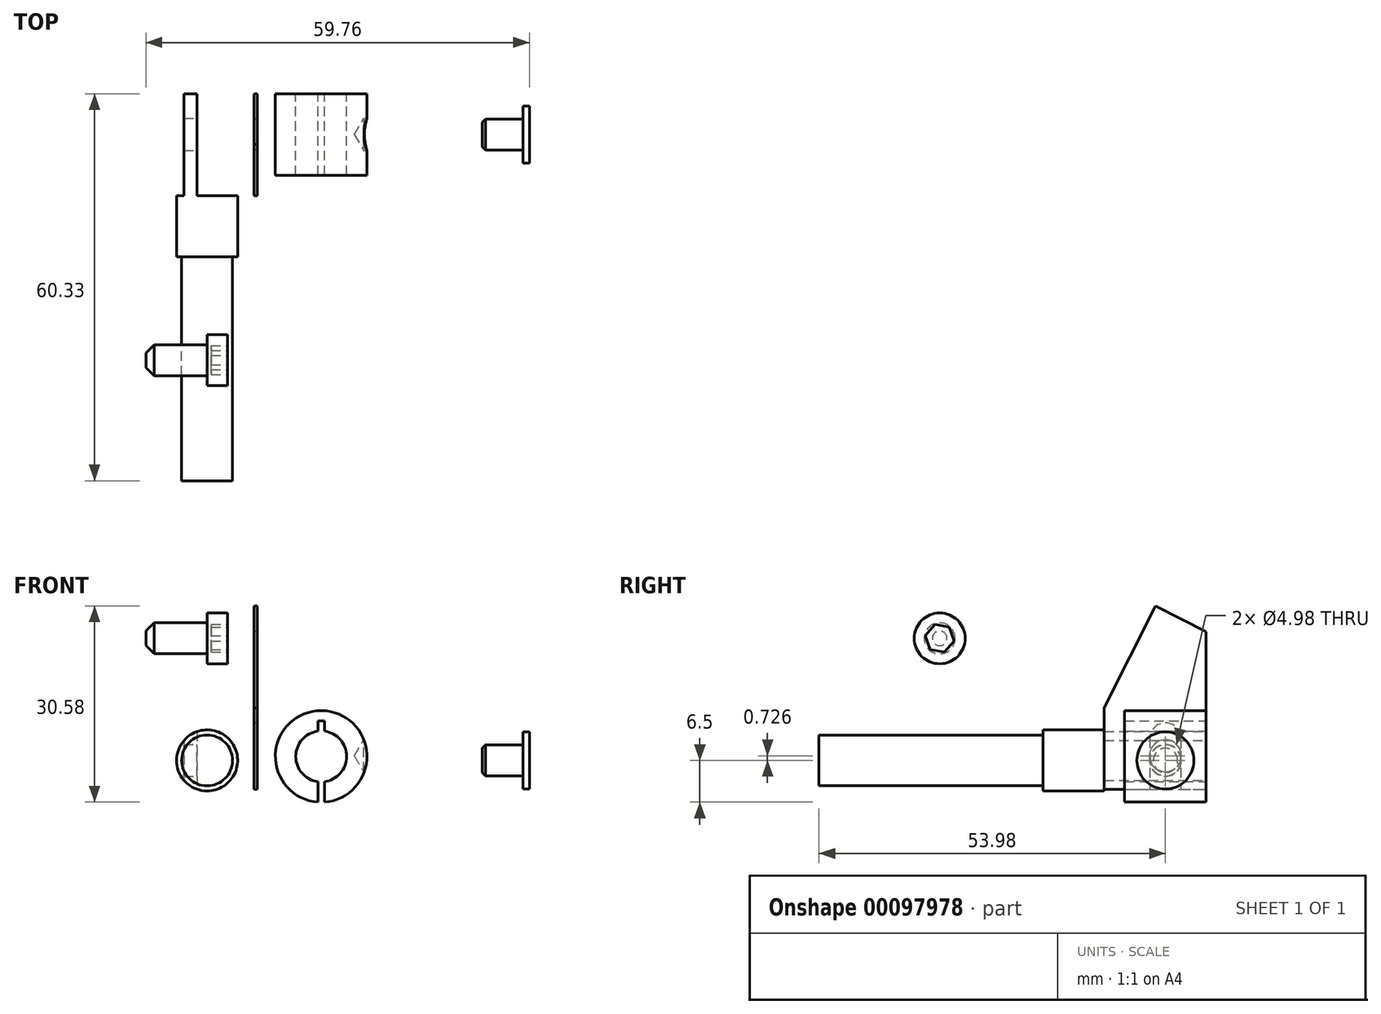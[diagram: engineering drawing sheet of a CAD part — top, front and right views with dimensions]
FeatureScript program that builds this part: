
annotation { "Feature Type Name" : "Feature", "Feature Type Description" : "" }
export const myFeature = defineFeature(function(context is Context, id is Id, definition is map)
    precondition{}
    {
        {
            var Q0;
            Q0=qCreatedBy(makeId("Front.planeOp"),FACE);
            var sketch = newSketch(context, id + "F0", { "sketchPlane" : qUnion([Q0])});
            skCircle(sketch, "E0", {"center": v(0, 0) * mm, "radius": 4.76 * mm});
            skSolve(sketch);
        }
        {
            var Q0;
            Q0=makeQuery(id+"F0.imprint","IMPRINT",FACE,{"disambiguationData":[TD([[makeQuery(id+"F0.imprint","IMPRINT",EDGE,{"derivedFrom":sQuery(id+"F0.wireOp",EDGE,"E0")}),1.0]])]});
            extrude(context, id + "F1", {"entities" : qUnion([Q0]), "depth" : 25.4 * mm});
        }
        {
            var Q0;
            Q0=makeQuery(id+"F1.opExtrude","CAP_FACE",FACE,{"disambiguationData":[OSD([sQuery(id+"F0.wireOp",EDGE,"E0")])],"isStart":false});
            var sketch = newSketch(context, id + "F2", { "sketchPlane" : qUnion([Q0])});
            skCircle(sketch, "E1.0", {"center": v(0, 0) * mm, "radius": 4.76 * mm, "construction": true});
            skCircle(sketch, "E2", {"center": v(0, 0) * mm, "radius": 3.96 * mm});
            skSolve(sketch);
        }
        {
            var Q0;
            Q0=makeQuery(id+"F2.imprint","IMPRINT",FACE,{"disambiguationData":[TD([[makeQuery(id+"F2.imprint","IMPRINT",EDGE,{"derivedFrom":sQuery(id+"F2.wireOp",EDGE,"E2")}),1.0]])]});
            extrude(context, id + "F3", {"entities" : qUnion([Q0]), "operationType" : NewBodyOperationType.ADD, "depth" : 34.92 * mm});
        }
        {
            var Q0;
            Q0=makeQuery(id+"F1.opExtrude","CAP_FACE",FACE,{"disambiguationData":[OSD([sQuery(id+"F0.wireOp",EDGE,"E0")])],"isStart":true});
            var sketch = newSketch(context, id + "F4", { "sketchPlane" : qUnion([Q0])});
            skLineSegment(sketch, "E3", {"start": v(1.59, 4.5) * mm, "end": v(1.59, -4.5) * mm});
            skArc(sketch, "E4.0", {"start": v(1.59, 4.5) * mm, "mid": v(-4.76, 0) * mm, "end": v(1.59, -4.5) * mm});
            skLineSegment(sketch, "E5", {"start": v(3.62, 3.1) * mm, "end": v(3.62, -3.1) * mm});
            skArc(sketch, "E6.trimOffspring", {"start": v(3.62, -3.1) * mm, "mid": v(4.76, 0) * mm, "end": v(3.62, 3.1) * mm});
            skSolve(sketch);
        }
        {
            var Q0;
            Q0=makeQuery(id+"F4.imprint","IMPRINT",FACE,{"disambiguationData":[TD([[makeQuery(id+"F4.imprint","IMPRINT",EDGE,{"derivedFrom":sQuery(id+"F4.wireOp",EDGE,"E3")}),-1.0]])]});
            var Q1;
            Q1=makeQuery(id+"F4.imprint","IMPRINT",FACE,{"disambiguationData":[TD([[makeQuery(id+"F4.imprint","IMPRINT",EDGE,{"derivedFrom":sQuery(id+"F4.wireOp",EDGE,"E5")}),1.0]])]});
            extrude(context, id + "F5", {"entities" : qUnion([Q0, Q1]), "operationType" : NewBodyOperationType.REMOVE, "oppositeDirection" : true, "depth" : 15.88 * mm});
        }
        {
            var Q0;
            Q0=makeQuery(id+"F5.boolean.opBoolean","COPY",FACE,{"derivedFrom":makeQuery(id+"F5.opExtrude","SWEPT_FACE",FACE,{"disambiguationData":[OSD([sQuery(id+"F4.wireOp",EDGE,"E3")])]})});
            var sketch = newSketch(context, id + "F6", { "sketchPlane" : qUnion([Q0])});
            skLineSegment(sketch, "E7", {"start": v(-6.35, 4.5) * mm, "end": v(-6.35, -4.5) * mm, "construction": true});
            skPoint(sketch, "E8", {"position": v(-6.35, 0) * mm});
            skSolve(sketch);
        }
        {
            var Q0;
            Q0=sQuery(id+"F6.wireOp",VERTEX,"E8");
            var Q1;
            Q1=makeQuery(id+"F1.opExtrude","SWEPT_BODY",BODY,{"disambiguationData":[OSD([sQuery(id+"F0.wireOp",EDGE,"E0")])]});
            hole(context, id + "F7", {"style" : HoleStyle.SIMPLE, "endStyle" : HoleEndStyle.THROUGH, "standardTappedOrClearance" : lookupTablePath({ "standard" : "ANSI", "fit" : "Close", "size" : "#10", "type" : "Clearance" }), "standardBlindInLast" : lookupTablePath({ "fit" : "Close", "standard" : "ANSI", "size" : "#10", "type" : "Clearance" }), "holeDiameter" : 4.98 * mm, "locations" : qUnion([Q0]), "scope" : qUnion([Q1]), "isTappedThrough" : true});
        }
        {
            var Q0;
            Q0=qCreatedBy(makeId("Front.planeOp"),FACE);
            var sketch = newSketch(context, id + "F8", { "sketchPlane" : qUnion([Q0])});
            skArc(sketch, "E9", {"start": v(18.29, -6.5) * mm, "mid": v(17.78, 7.76) * mm, "end": v(17.27, -6.5) * mm});
            skArc(sketch, "E10", {"start": v(17.27, 4.55) * mm, "mid": v(13.82, 0.62) * mm, "end": v(17.27, -3.3) * mm});
            skLineSegment(sketch, "E11", {"start": v(18.29, 6.18) * mm, "end": v(18.29, 4.55) * mm});
            skLineSegment(sketch, "E12", {"start": v(17.27, 6.18) * mm, "end": v(17.27, 4.55) * mm});
            skLineSegment(sketch, "E13", {"start": v(18.29, 6.18) * mm, "end": v(17.27, 6.18) * mm});
            skLineSegment(sketch, "E14.trimOffspring", {"start": v(18.29, -3.3) * mm, "end": v(18.29, -6.5) * mm});
            skLineSegment(sketch, "E15.trimOffspring", {"start": v(17.27, -3.3) * mm, "end": v(17.27, -6.5) * mm});
            skArc(sketch, "E16.trimOffspring", {"start": v(18.29, -3.3) * mm, "mid": v(21.74, 0.62) * mm, "end": v(18.29, 4.55) * mm});
            skSolve(sketch);
        }
        {
            var Q0;
            Q0=makeQuery(id+"F8.imprint","IMPRINT",FACE,{"disambiguationData":[TD([[makeQuery(id+"F8.imprint","IMPRINT",EDGE,{"derivedFrom":sQuery(id+"F8.wireOp",EDGE,"E9")}),1.0]])]});
            extrude(context, id + "F9", {"entities" : qUnion([Q0]), "depth" : 12.7 * mm});
        }
        {
            var Q0;
            Q0=qCreatedBy(makeId("Right.planeOp"),FACE);
            cPlane(context, id + "F10", {"entities" : qUnion([Q0]), "cplaneType" : CPlaneType.OFFSET, "offset" : 25.4 * mm, "width" : 152.4 * mm, "height" : 152.4 * mm});
        }
        {
            var Q0;
            Q0=qCreatedBy(id+"F10.planeOp",FACE);
            var sketch = newSketch(context, id + "F11", { "sketchPlane" : qUnion([Q0])});
            skLineSegment(sketch, "E17", {"start": v(-12.7, 7.76) * mm, "end": v(0, 7.76) * mm, "construction": true});
            skLineSegment(sketch, "E18", {"start": v(-6.35, 7.76) * mm, "end": v(-6.35, -6.3) * mm, "construction": true});
            skPoint(sketch, "E19", {"position": v(-6.35, 0.73) * mm});
            skSolve(sketch);
        }
        {
            var Q0;
            Q0=sQuery(id+"F11.wireOp",VERTEX,"E19");
            var Q1;
            Q1=makeQuery(id+"F9.opExtrude","SWEPT_BODY",BODY,{"disambiguationData":[OSD([sQuery(id+"F8.wireOp",EDGE,"E9"),sQuery(id+"F8.wireOp",EDGE,"E10"),sQuery(id+"F8.wireOp",EDGE,"E11"),sQuery(id+"F8.wireOp",EDGE,"E12"),sQuery(id+"F8.wireOp",EDGE,"E13"),sQuery(id+"F8.wireOp",EDGE,"E14.trimOffspring"),sQuery(id+"F8.wireOp",EDGE,"E15.trimOffspring"),sQuery(id+"F8.wireOp",EDGE,"E16.trimOffspring")])]});
            hole(context, id + "F12", {"style" : HoleStyle.SIMPLE, "endStyle" : HoleEndStyle.BLIND, "standardTappedOrClearance" : lookupTablePath({ "standard" : "ANSI", "fit" : "Close", "size" : "#10", "type" : "Clearance" }), "standardBlindInLast" : lookupTablePath({ "fit" : "Close", "standard" : "ANSI", "size" : "#10", "type" : "Clearance" }), "holeDiameter" : 4.98 * mm, "holeDepth" : 0.03 * mm, "locations" : qUnion([Q0]), "scope" : qUnion([Q1])});
        }
        {
            var Q0;
            Q0=makeQuery(id+"F5.boolean.opBoolean","COPY",FACE,{"derivedFrom":makeQuery(id+"F5.opExtrude","SWEPT_FACE",FACE,{"disambiguationData":[OSD([sQuery(id+"F4.wireOp",EDGE,"E3")])]})});
            cPlane(context, id + "F13", {"entities" : qUnion([Q0]), "cplaneType" : CPlaneType.OFFSET, "offset" : 50.8 * mm, "width" : 152.4 * mm, "height" : 152.4 * mm});
        }
        {
            var Q0;
            Q0=qCreatedBy(id+"F13.planeOp",FACE);
            var sketch = newSketch(context, id + "F14", { "sketchPlane" : qUnion([Q0])});
            skCircle(sketch, "E20.0", {"center": v(-6.35, 0) * mm, "radius": 2.49 * mm, "construction": true});
            skCircle(sketch, "E21", {"center": v(-6.35, 0) * mm, "radius": 4.45 * mm});
            skSolve(sketch);
        }
        {
            var Q0;
            Q0=makeQuery(id+"F14.imprint","IMPRINT",FACE,{"disambiguationData":[TD([[makeQuery(id+"F14.imprint","IMPRINT",EDGE,{"derivedFrom":sQuery(id+"F14.wireOp",EDGE,"E21")}),1.0]])]});
            extrude(context, id + "F15", {"entities" : qUnion([Q0]), "depth" : 1.02 * mm});
        }
        {
            var Q0;
            Q0=makeQuery(id+"F15.opExtrude","CAP_FACE",FACE,{"disambiguationData":[OSD([sQuery(id+"F14.wireOp",EDGE,"E21")])],"isStart":true});
            var sketch = newSketch(context, id + "F16", { "sketchPlane" : qUnion([Q0])});
            skCircle(sketch, "E22.0", {"center": v(6.35, 0) * mm, "radius": 4.45 * mm, "construction": true});
            skCircle(sketch, "E23", {"center": v(6.35, 0) * mm, "radius": 2.41 * mm});
            skSolve(sketch);
        }
        {
            var Q0;
            Q0=makeQuery(id+"F16.imprint","IMPRINT",FACE,{"disambiguationData":[TD([[makeQuery(id+"F16.imprint","IMPRINT",EDGE,{"derivedFrom":sQuery(id+"F16.wireOp",EDGE,"E23")}),1.0]])]});
            extrude(context, id + "F17", {"entities" : qUnion([Q0]), "operationType" : NewBodyOperationType.ADD, "depth" : 6.35 * mm});
        }
        {
            var Q0;
            Q0=makeQuery(id+"F17.opExtrude","CAP_EDGE",EDGE,{"disambiguationData":[OSD([sQuery(id+"F16.wireOp",EDGE,"E23")])],"isStart":false});
            chamfer(context, id + "F18", {"entities" : qUnion([Q0]), "width" : 0.5 * mm, "tangentPropagation" : true});
        }
        {
            var Q0;
            Q0=makeQuery(id+"F5.boolean.opBoolean","COPY",FACE,{"derivedFrom":makeQuery(id+"F5.opExtrude","SWEPT_FACE",FACE,{"disambiguationData":[OSD([sQuery(id+"F4.wireOp",EDGE,"E3")])]})});
            cPlane(context, id + "F19", {"entities" : qUnion([Q0]), "cplaneType" : CPlaneType.OFFSET, "offset" : 8.9 * mm, "width" : 152.4 * mm, "height" : 152.4 * mm});
        }
        {
            var Q0;
            Q0=qCreatedBy(id+"F19.planeOp",FACE);
            var sketch = newSketch(context, id + "F20", { "sketchPlane" : qUnion([Q0])});
            skLineSegment(sketch, "E24.0.0", {"start": v(0, -4.5) * mm, "end": v(0, 4.5) * mm, "construction": true});
            skLineSegment(sketch, "E24.0.1", {"start": v(0, 4.5) * mm, "end": v(-15.88, 4.5) * mm, "construction": true});
            skLineSegment(sketch, "E24.0.2", {"start": v(-15.88, 4.5) * mm, "end": v(-15.88, -4.5) * mm, "construction": true});
            skLineSegment(sketch, "E24.0.3", {"start": v(-15.88, -4.5) * mm, "end": v(0, -4.5) * mm, "construction": true});
            skLineSegment(sketch, "E25.bottom", {"start": v(-15.88, -4.5) * mm, "end": v(0, -4.5) * mm});
            skLineSegment(sketch, "E25.left", {"start": v(-15.88, -4.5) * mm, "end": v(-15.88, 8.2) * mm});
            skLineSegment(sketch, "E25.right", {"start": v(0, -4.5) * mm, "end": v(0, 20.05) * mm});
            skArc(sketch, "E26.0", {"start": v(-8.1, 1.77) * mm, "mid": v(-4.69, -1.85) * mm, "end": v(-7.92, 1.93) * mm, "construction": true});
            skLineSegment(sketch, "E27", {"start": v(-15.88, 3.43) * mm, "end": v(0, 3.43) * mm, "construction": true});
            skLineSegment(sketch, "E28", {"start": v(-6.35, 0) * mm, "end": v(-6.35, 3.43) * mm, "construction": true});
            skLineSegment(sketch, "E29", {"start": v(-8.76, 3.43) * mm, "end": v(-8.76, -4.5) * mm});
            skLineSegment(sketch, "E30", {"start": v(-3.94, 3.43) * mm, "end": v(-3.94, -4.5) * mm});
            skLineSegment(sketch, "E31", {"start": v(-7.92, 24.08) * mm, "end": v(-7.92, 1.93) * mm, "construction": true});
            skLineSegment(sketch, "E32", {"start": v(-15.88, 8.2) * mm, "end": v(0, 8.2) * mm, "construction": true});
            skLineSegment(sketch, "E33", {"start": v(-7.92, 24.08) * mm, "end": v(-15.88, 8.2) * mm});
            skArc(sketch, "E34.trimOffspring", {"start": v(-3.94, 3.43) * mm, "mid": v(-6.35, 5.85) * mm, "end": v(-8.76, 3.43) * mm});
            skLineSegment(sketch, "E35.trimOffspring", {"start": v(-7.92, 1.6) * mm, "end": v(-7.92, -4.5) * mm, "construction": true});
            skLineSegment(sketch, "E36", {"start": v(-7.92, 24.08) * mm, "end": v(0, 20.05) * mm});
            skLineSegment(sketch, "E37", {"start": v(-7.92, 24.08) * mm, "end": v(-16.9, 24.08) * mm, "construction": true});
            skSolve(sketch);
        }
        {
            var Q0;
            {var subQ0=sQuery(id+"F20.wireOp",EDGE,"E25.left");Q0=makeQuery(id+"F20.imprint","IMPRINT",FACE,{"disambiguationData":[TD([[makeQuery(id+"F20.imprint","IMPRINT",EDGE,{"derivedFrom":subQ0}),-1.0]])]});}
            extrude(context, id + "F21", {"entities" : qUnion([Q0]), "depth" : 0.5 * mm});
        }
        {
            var Q0;
            Q0=qCreatedBy(makeId("Right.planeOp"),FACE);
            var sketch = newSketch(context, id + "F22", { "sketchPlane" : qUnion([Q0])});
            skCircle(sketch, "E38", {"center": v(-41.53, 19.03) * mm, "radius": 3.96 * mm});
            skSolve(sketch);
        }
        {
            var Q0;
            Q0=makeQuery(id+"F22.imprint","IMPRINT",FACE,{"disambiguationData":[TD([[makeQuery(id+"F22.imprint","IMPRINT",EDGE,{"derivedFrom":sQuery(id+"F22.wireOp",EDGE,"E38")}),1.0]])]});
            extrude(context, id + "F23", {"entities" : qUnion([Q0]), "depth" : 3.17 * mm});
        }
        {
            var Q0;
            Q0=makeQuery(id+"F23.opExtrude","CAP_FACE",FACE,{"disambiguationData":[OSD([sQuery(id+"F22.wireOp",EDGE,"E38")])],"isStart":false});
            var sketch = newSketch(context, id + "F24", { "sketchPlane" : qUnion([Q0])});
            skCircle(sketch, "E39.0", {"center": v(-41.53, 19.03) * mm, "radius": 3.96 * mm, "construction": true});
            skCircle(sketch, "E40.cCircle", {"center": v(-41.53, 19.03) * mm, "radius": 1.98 * mm, "construction": true});
            skLineSegment(sketch, "E40.0", {"start": v(-39.28, 18.6) * mm, "end": v(-40.78, 16.86) * mm});
            skLineSegment(sketch, "E40.1", {"start": v(-40.78, 16.86) * mm, "end": v(-43.03, 17.3) * mm});
            skLineSegment(sketch, "E40.2", {"start": v(-43.03, 17.3) * mm, "end": v(-43.77, 19.46) * mm});
            skLineSegment(sketch, "E40.3", {"start": v(-43.77, 19.46) * mm, "end": v(-42.28, 21.19) * mm});
            skLineSegment(sketch, "E40.4", {"start": v(-42.28, 21.19) * mm, "end": v(-40.03, 20.75) * mm});
            skLineSegment(sketch, "E40.5", {"start": v(-40.03, 20.75) * mm, "end": v(-39.28, 18.6) * mm});
            skPoint(sketch, "E40.0.midPoint", {"position": v(-40.03, 17.73) * mm});
            skSolve(sketch);
        }
        {
            var Q0;
            Q0=makeQuery(id+"F24.imprint","IMPRINT",FACE,{"disambiguationData":[TD([[makeQuery(id+"F24.imprint","IMPRINT",EDGE,{"derivedFrom":sQuery(id+"F24.wireOp",EDGE,"E40.0")}),-1.0]])]});
            extrude(context, id + "F25", {"entities" : qUnion([Q0]), "operationType" : NewBodyOperationType.REMOVE, "oppositeDirection" : true, "depth" : 2.54 * mm});
        }
        {
            var Q0;
            Q0=makeQuery(id+"F23.opExtrude","CAP_FACE",FACE,{"disambiguationData":[OSD([sQuery(id+"F22.wireOp",EDGE,"E38")])],"isStart":true});
            var sketch = newSketch(context, id + "F26", { "sketchPlane" : qUnion([Q0])});
            skCircle(sketch, "E41.0", {"center": v(41.53, 19.03) * mm, "radius": 3.96 * mm, "construction": true});
            skCircle(sketch, "E42", {"center": v(41.53, 19.03) * mm, "radius": 2.41 * mm});
            skSolve(sketch);
        }
        {
            var Q0;
            Q0=makeQuery(id+"F26.imprint","IMPRINT",FACE,{"disambiguationData":[TD([[makeQuery(id+"F26.imprint","IMPRINT",EDGE,{"derivedFrom":sQuery(id+"F26.wireOp",EDGE,"E42")}),1.0]])]});
            extrude(context, id + "F27", {"entities" : qUnion([Q0]), "operationType" : NewBodyOperationType.ADD, "depth" : 9.52 * mm});
        }
        {
            var Q0;
            Q0=makeQuery(id+"F27.opExtrude","CAP_EDGE",EDGE,{"disambiguationData":[OSD([sQuery(id+"F26.wireOp",EDGE,"E42")])],"isStart":false});
            chamfer(context, id + "F28", {"entities" : qUnion([Q0]), "width" : 1.27 * mm, "tangentPropagation" : true});
        }
    });
